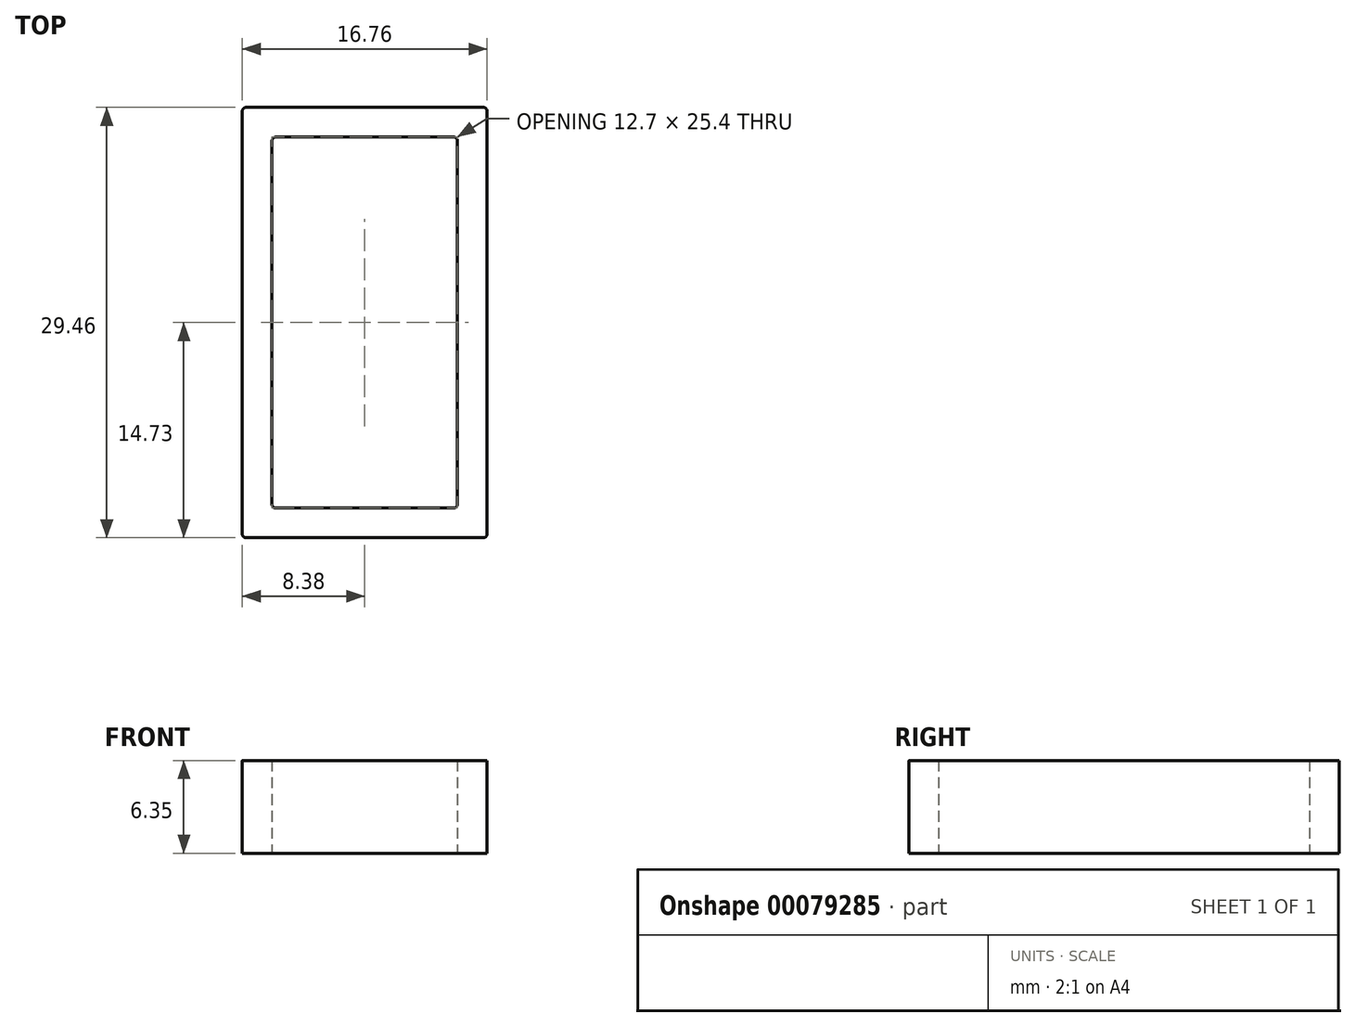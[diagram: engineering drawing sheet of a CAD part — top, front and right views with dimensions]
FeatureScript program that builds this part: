
annotation { "Feature Type Name" : "Feature", "Feature Type Description" : "" }
export const myFeature = defineFeature(function(context is Context, id is Id, definition is map)
    precondition{}
    {
        {
            var Q0;
            Q0=qCreatedBy(makeId("Top.planeOp"),FACE);
            var sketch = newSketch(context, id + "F0", { "sketchPlane" : qUnion([Q0])});
            skLineSegment(sketch, "E0.bottom", {"start": v(0, 0) * mm, "end": v(12.7, 0) * mm});
            skLineSegment(sketch, "E0.top", {"start": v(0, 25.4) * mm, "end": v(12.7, 25.4) * mm});
            skLineSegment(sketch, "E0.left", {"start": v(0, 0) * mm, "end": v(0, 25.4) * mm});
            skLineSegment(sketch, "E0.right", {"start": v(12.7, 0) * mm, "end": v(12.7, 25.4) * mm});
            skLineSegment(sketch, "E1.0", {"start": v(-2.03, -2.03) * mm, "end": v(-2.03, 27.43) * mm});
            skLineSegment(sketch, "E1.1", {"start": v(-2.03, -2.03) * mm, "end": v(14.73, -2.03) * mm});
            skLineSegment(sketch, "E1.2", {"start": v(14.73, -2.03) * mm, "end": v(14.73, 27.43) * mm});
            skLineSegment(sketch, "E1.3", {"start": v(-2.03, 27.43) * mm, "end": v(14.73, 27.43) * mm});
            skSolve(sketch);
        }
        {
            var Q0;
            Q0 = qSketchRegion(id + "F0", true);
            extrude(context, id + "F1", {"entities" : qUnion([Q0]), "depth" : 6.35 * mm});
        }
        {
            var Q0;
            Q0=makeQuery(id+"F1.opExtrude","SWEPT_EDGE",EDGE,{"disambiguationData":[OSD([sQuery(id+"F0.wireOp",EDGE,"E1.1"),sQuery(id+"F0.wireOp",EDGE,"E1.2")])]});
            var Q1;
            Q1=makeQuery(id+"F1.opExtrude","SWEPT_EDGE",EDGE,{"disambiguationData":[OSD([sQuery(id+"F0.wireOp",EDGE,"E1.0"),sQuery(id+"F0.wireOp",EDGE,"E1.1")])]});
            var Q2;
            Q2=makeQuery(id+"F1.opExtrude","SWEPT_EDGE",EDGE,{"disambiguationData":[OSD([sQuery(id+"F0.wireOp",EDGE,"E1.2"),sQuery(id+"F0.wireOp",EDGE,"E1.3")])]});
            var Q3;
            Q3=makeQuery(id+"F1.opExtrude","SWEPT_EDGE",EDGE,{"disambiguationData":[OSD([sQuery(id+"F0.wireOp",EDGE,"E1.0"),sQuery(id+"F0.wireOp",EDGE,"E1.3")])]});
            var Q4;
            Q4=makeQuery(id+"F1.opExtrude","SWEPT_EDGE",EDGE,{"disambiguationData":[OSD([sQuery(id+"F0.wireOp",EDGE,"E0.bottom"),sQuery(id+"F0.wireOp",EDGE,"E0.right")])]});
            var Q5;
            Q5=makeQuery(id+"F1.opExtrude","SWEPT_EDGE",EDGE,{"disambiguationData":[OSD([sQuery(id+"F0.wireOp",EDGE,"E0.top"),sQuery(id+"F0.wireOp",EDGE,"E0.right")])]});
            var Q6;
            Q6=makeQuery(id+"F1.opExtrude","SWEPT_EDGE",EDGE,{"disambiguationData":[OSD([sQuery(id+"F0.wireOp",EDGE,"E0.top"),sQuery(id+"F0.wireOp",EDGE,"E0.left")])]});
            var Q7;
            Q7=makeQuery(id+"F1.opExtrude","SWEPT_EDGE",EDGE,{"disambiguationData":[OSD([sQuery(id+"F0.wireOp",EDGE,"E0.bottom"),sQuery(id+"F0.wireOp",EDGE,"E0.left")])]});
            fillet(context, id + "F2", {"entities" : qUnion([Q0, Q1, Q2, Q3, Q4, Q5, Q6, Q7]), "radius" : 0.25 * mm, "tangentPropagation" : true, "allowEdgeOverflow" : false});
        }
    });
